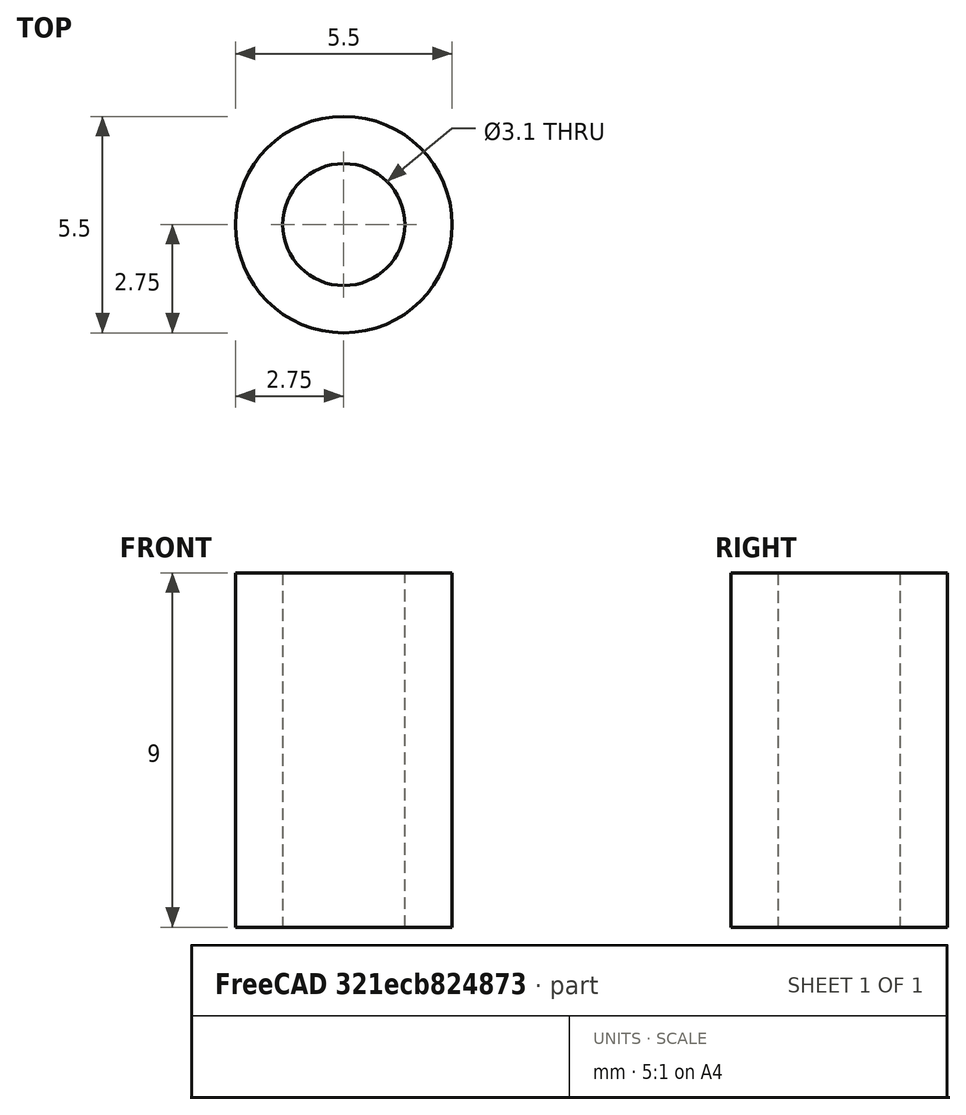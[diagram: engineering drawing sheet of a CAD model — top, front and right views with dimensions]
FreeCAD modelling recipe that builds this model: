
FCSTD DOCUMENT  (FreeCAD 1.0R38641 +468 (Git))
Label: k1_toolhead_cover_experimental_spacer
License: All rights reserved
LicenseURL: https://en.wikipedia.org/wiki/All_rights_reserved
objects: Sketcher::SketchObject×1, PartDesign::Pad×1, PartDesign::Body×1
note: 6 computed .brp shape members not serialized (recipe doc carries the construction recipe); baked Part::Feature solids carry a one-line shape summary decoded from their .brp

FEATURE [Sketcher::SketchObject] Sketch
  ArcFitTolerance = 1e-06
  AttachmentSupport = -> [XY_Plane]
  FullyConstrained = true
  MakeInternals = false
  MapMode = 5
  sketch-geometry (2):
    g0: Circle CenterX=0 CenterY=0 CenterZ=0 NormalX=0 NormalY=0 NormalZ=1 AngleXU=0 Radius=1.55
    g1: Circle CenterX=0 CenterY=0 CenterZ=0 NormalX=0 NormalY=0 NormalZ=1 AngleXU=0 Radius=2.75
  constraints (4):
    c: Coincident(g0,g-1)
    c: Coincident(g1,g0)
    c: Diameter(g0) = 3.1
    c: Diameter(g1) = 5.5
FEATURE [PartDesign::Pad] Pad
  Direction = (0,0,1)
  Length = 9
  Length2 = 10
  Profile = -> Sketch
  ReferenceAxis = -> Sketch [N_Axis]
  Refine = true
  Suppressed = false
  Type = 0
FEATURE [PartDesign::Body] Body  label="k1_toolhead_cover_experimental_spacer"
  AllowCompound = false
  Group = -> [Sketch,Pad]
  Origin = -> Origin
  Tip = -> Pad
